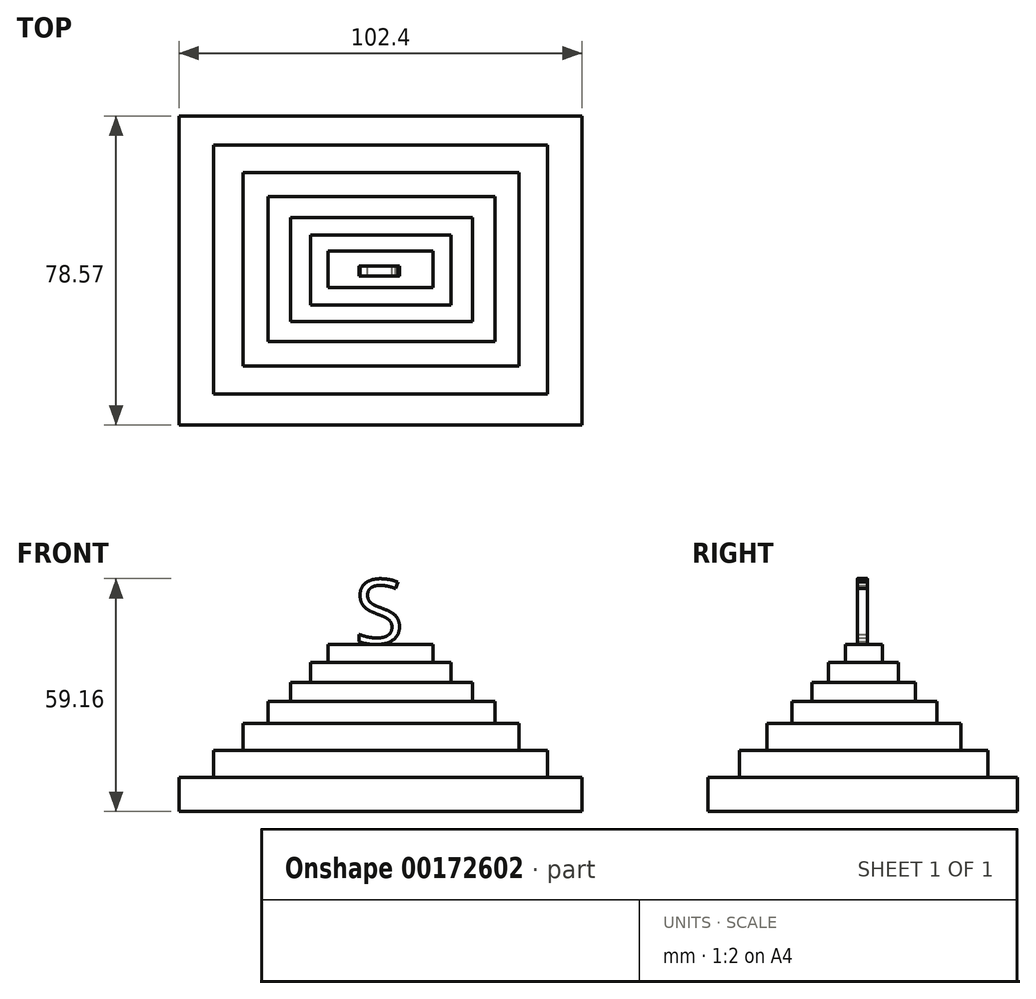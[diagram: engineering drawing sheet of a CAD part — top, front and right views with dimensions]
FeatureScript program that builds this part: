
annotation { "Feature Type Name" : "Feature", "Feature Type Description" : "" }
export const myFeature = defineFeature(function(context is Context, id is Id, definition is map)
    precondition{}
    {
        {
            var Q0;
            Q0=qCreatedBy(makeId("Top.planeOp"),FACE);
            var sketch = newSketch(context, id + "F0", { "sketchPlane" : qUnion([Q0])});
            skLineSegment(sketch, "E0.bottom", {"start": v(-50.86, 38.1) * mm, "end": v(51.54, 38.1) * mm});
            skLineSegment(sketch, "E0.top", {"start": v(-50.86, -40.47) * mm, "end": v(51.54, -40.47) * mm});
            skLineSegment(sketch, "E0.left", {"start": v(-50.86, 38.1) * mm, "end": v(-50.86, -40.47) * mm});
            skLineSegment(sketch, "E0.right", {"start": v(51.54, 38.1) * mm, "end": v(51.54, -40.47) * mm});
            skSolve(sketch);
        }
        {
            var Q0;
            Q0 = qSketchRegion(id + "F0", true);
            var Q1;
            Q1 = qSketchRegion(id + "FIFzSHws54il2H1_1", true);
            extrude(context, id + "F1", {"entities" : qUnion([Q0, Q1]), "depth" : 8.64 * mm});
        }
        {
            var Q0;
            Q0=qCreatedBy(makeId("Top.planeOp"),FACE);
            var sketch = newSketch(context, id + "F2", { "sketchPlane" : qUnion([Q0])});
            skLineSegment(sketch, "E1.bottom", {"start": v(-42.07, 30.67) * mm, "end": v(42.75, 30.67) * mm});
            skLineSegment(sketch, "E1.top", {"start": v(-42.07, -32.53) * mm, "end": v(42.75, -32.53) * mm});
            skLineSegment(sketch, "E1.left", {"start": v(-42.07, 30.67) * mm, "end": v(-42.07, -32.53) * mm});
            skLineSegment(sketch, "E1.right", {"start": v(42.75, 30.67) * mm, "end": v(42.75, -32.53) * mm});
            skSolve(sketch);
        }
        {
            var Q0;
            Q0 = qSketchRegion(id + "F2", true);
            extrude(context, id + "F3", {"entities" : qUnion([Q0]), "operationType" : NewBodyOperationType.ADD, "depth" : 15.5 * mm});
        }
        {
            var Q0;
            Q0=qCreatedBy(makeId("Top.planeOp"),FACE);
            var sketch = newSketch(context, id + "F4", { "sketchPlane" : qUnion([Q0])});
            skLineSegment(sketch, "E2.bottom", {"start": v(-34.64, 23.74) * mm, "end": v(35.48, 23.74) * mm});
            skLineSegment(sketch, "E2.top", {"start": v(-34.64, -25.43) * mm, "end": v(35.48, -25.43) * mm});
            skLineSegment(sketch, "E2.left", {"start": v(-34.64, 23.74) * mm, "end": v(-34.64, -25.43) * mm});
            skLineSegment(sketch, "E2.right", {"start": v(35.48, 23.74) * mm, "end": v(35.48, -25.43) * mm});
            skSolve(sketch);
        }
        {
            var Q0;
            Q0 = qSketchRegion(id + "F4", true);
            extrude(context, id + "F5", {"entities" : qUnion([Q0]), "operationType" : NewBodyOperationType.ADD, "depth" : 22.35 * mm});
        }
        {
            var Q0;
            Q0=qCreatedBy(makeId("Top.planeOp"),FACE);
            var sketch = newSketch(context, id + "F6", { "sketchPlane" : qUnion([Q0])});
            skLineSegment(sketch, "E3.bottom", {"start": v(-28.22, 17.66) * mm, "end": v(29.4, 17.66) * mm});
            skLineSegment(sketch, "E3.top", {"start": v(-28.22, -19.18) * mm, "end": v(29.4, -19.18) * mm});
            skLineSegment(sketch, "E3.left", {"start": v(-28.22, 17.66) * mm, "end": v(-28.22, -19.18) * mm});
            skLineSegment(sketch, "E3.right", {"start": v(29.4, 17.66) * mm, "end": v(29.4, -19.18) * mm});
            skSolve(sketch);
        }
        {
            var Q0;
            Q0 = qSketchRegion(id + "F6", true);
            extrude(context, id + "F7", {"entities" : qUnion([Q0]), "operationType" : NewBodyOperationType.ADD, "depth" : 27.94 * mm});
        }
        {
            var Q0;
            Q0=qCreatedBy(makeId("Top.planeOp"),FACE);
            var sketch = newSketch(context, id + "F8", { "sketchPlane" : qUnion([Q0])});
            skLineSegment(sketch, "E4.bottom", {"start": v(-22.47, 12.25) * mm, "end": v(23.66, 12.25) * mm});
            skLineSegment(sketch, "E4.top", {"start": v(-22.47, -14.1) * mm, "end": v(23.66, -14.1) * mm});
            skLineSegment(sketch, "E4.left", {"start": v(-22.47, 12.25) * mm, "end": v(-22.47, -14.1) * mm});
            skLineSegment(sketch, "E4.right", {"start": v(23.66, 12.25) * mm, "end": v(23.66, -14.1) * mm});
            skSolve(sketch);
        }
        {
            var Q0;
            Q0 = qSketchRegion(id + "F8", true);
            extrude(context, id + "F9", {"entities" : qUnion([Q0]), "operationType" : NewBodyOperationType.ADD, "depth" : 32.77 * mm});
        }
        {
            var Q0;
            Q0=qCreatedBy(makeId("Top.planeOp"),FACE);
            var sketch = newSketch(context, id + "F10", { "sketchPlane" : qUnion([Q0])});
            skLineSegment(sketch, "E5.bottom", {"start": v(-17.4, 7.86) * mm, "end": v(18.25, 7.86) * mm});
            skLineSegment(sketch, "E5.top", {"start": v(-17.4, -9.89) * mm, "end": v(18.25, -9.89) * mm});
            skLineSegment(sketch, "E5.left", {"start": v(-17.4, 7.86) * mm, "end": v(-17.4, -9.89) * mm});
            skLineSegment(sketch, "E5.right", {"start": v(18.25, 7.86) * mm, "end": v(18.25, -9.89) * mm});
            skSolve(sketch);
        }
        {
            var Q0;
            Q0 = qSketchRegion(id + "F10", true);
            extrude(context, id + "F11", {"entities" : qUnion([Q0]), "operationType" : NewBodyOperationType.ADD, "depth" : 37.85 * mm});
        }
        {
            var Q0;
            Q0=qCreatedBy(makeId("Top.planeOp"),FACE);
            var sketch = newSketch(context, id + "F12", { "sketchPlane" : qUnion([Q0])});
            skLineSegment(sketch, "E6.bottom", {"start": v(-13.01, 3.8) * mm, "end": v(13.69, 3.8) * mm});
            skLineSegment(sketch, "E6.top", {"start": v(-13.01, -5.5) * mm, "end": v(13.69, -5.5) * mm});
            skLineSegment(sketch, "E6.left", {"start": v(-13.01, 3.8) * mm, "end": v(-13.01, -5.5) * mm});
            skLineSegment(sketch, "E6.right", {"start": v(13.69, 3.8) * mm, "end": v(13.69, -5.5) * mm});
            skSolve(sketch);
        }
        {
            var Q0;
            Q0 = qSketchRegion(id + "F12", true);
            extrude(context, id + "F13", {"entities" : qUnion([Q0]), "operationType" : NewBodyOperationType.ADD, "depth" : 42.42 * mm});
        }
        {
            var Q0;
            Q0=qCreatedBy(makeId("Front.planeOp"),FACE);
            var sketch = newSketch(context, id + "F14", { "sketchPlane" : qUnion([Q0])});
            skArc(sketch, "E7", {"start": v(7.77, 42.5) * mm, "mid": v(0, 59.5) * mm, "end": v(-7.77, 42.5) * mm});
            skSolve(sketch);
        }
        {
            var Q0;
            Q0 = qSketchRegion(id + "F14", true);
            var Q1;
            Q1=sQuery(id+"F14.wireOp",EDGE,"E7");
            extrude(context, id + "F15", {"entities" : qUnion([Q0]), "bodyType" : ToolBodyType.SURFACE, "surfaceEntities" : qUnion([Q1]), "depth" : 3.3 * mm});
        }
        {
            var Q0;
            Q0 = qSketchRegion(id + "F14", true);
            var Q1;
            Q1 = qConstructionFilter(qBodyType(qCreatedBy(id + "F14" ,EDGE), BodyType.WIRE), ConstructionObject.NO);
            extrude(context, id + "F16", {"entities" : qUnion([Q0]), "bodyType" : ToolBodyType.SURFACE, "surfaceEntities" : qUnion([Q1]), "oppositeDirection" : true, "depth" : 1.52 * mm});
        }
        {
            var Q0;
            Q0=qCreatedBy(makeId("Front.planeOp"),FACE);
            var sketch = newSketch(context, id + "F17", { "sketchPlane" : qUnion([Q0])});
            skText(sketch, "E8", { "text": "S", "fontName": "OpenSans-Regular.ttf"});
            const initialGuessF17  = {"E8": [-0.00625, 0.04267, 1, 0, 0.0164]};
            skSetInitialGuess(sketch, initialGuessF17);
            skSolve(sketch);
        }
        {
            var Q0;
            Q0 = qSketchRegion(id + "F17", true);
            extrude(context, id + "F18", {"entities" : qUnion([Q0]), "depth" : 2.54 * mm});
        }
    });
